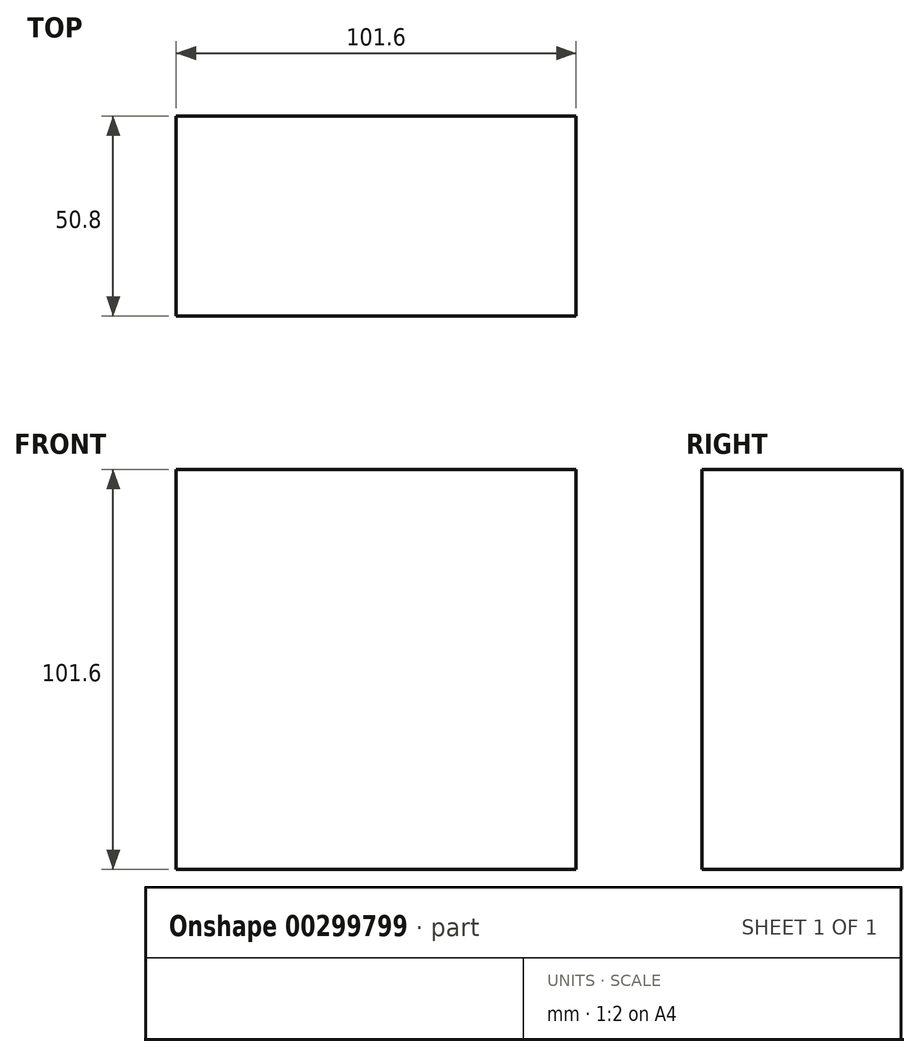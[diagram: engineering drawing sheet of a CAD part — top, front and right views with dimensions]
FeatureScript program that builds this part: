
annotation { "Feature Type Name" : "Feature", "Feature Type Description" : "" }
export const myFeature = defineFeature(function(context is Context, id is Id, definition is map)
    precondition{}
    {
        {
            var Q0;
            Q0=qCreatedBy(makeId("Front.planeOp"),FACE);
            var sketch = newSketch(context, id + "F0", { "sketchPlane" : qUnion([Q0])});
            skLineSegment(sketch, "E0.bottom", {"start": v(-50.8, 50.8) * mm, "end": v(50.8, 50.8) * mm});
            skLineSegment(sketch, "E0.top", {"start": v(-50.8, -50.8) * mm, "end": v(50.8, -50.8) * mm});
            skLineSegment(sketch, "E0.left", {"start": v(-50.8, 50.8) * mm, "end": v(-50.8, -50.8) * mm});
            skLineSegment(sketch, "E0.right", {"start": v(50.8, 50.8) * mm, "end": v(50.8, -50.8) * mm});
            skPoint(sketch, "E0.middle", {"position": v(0, 0) * mm});
            skSolve(sketch);
        }
        {
            var Q0;
            Q0=makeQuery(id+"F0.imprint","IMPRINT",FACE,{"disambiguationData":[TD([[makeQuery(id+"F0.imprint","IMPRINT",EDGE,{"derivedFrom":sQuery(id+"F0.wireOp",EDGE,"E0.bottom")}),-1.0]])]});
            extrude(context, id + "F1", {"entities" : qUnion([Q0]), "depth" : 50.8 * mm});
        }
    });
